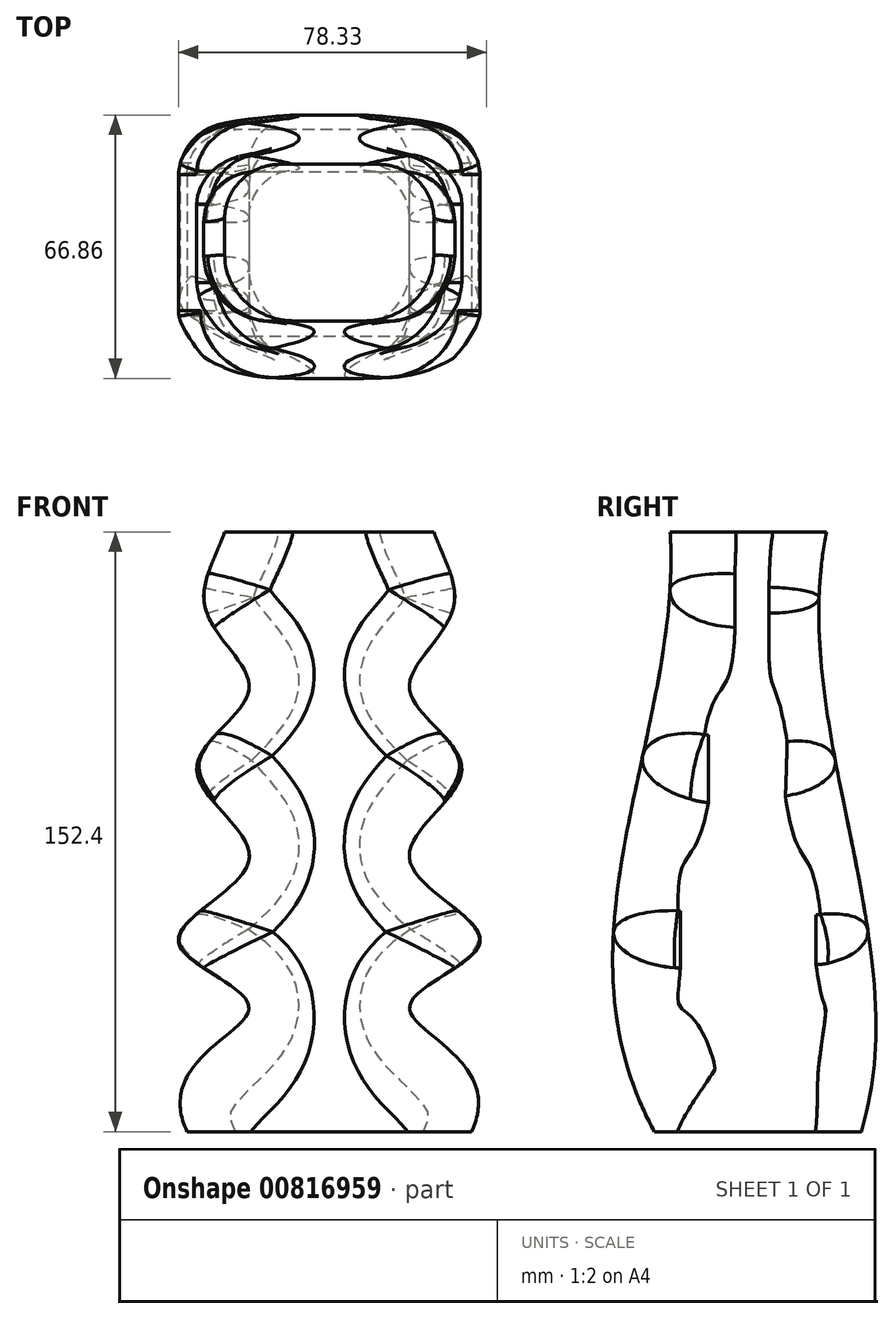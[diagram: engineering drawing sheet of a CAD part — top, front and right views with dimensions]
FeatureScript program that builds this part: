
annotation { "Feature Type Name" : "Feature", "Feature Type Description" : "" }
export const myFeature = defineFeature(function(context is Context, id is Id, definition is map)
    precondition{}
    {
        {
            var Q0;
            Q0=qCreatedBy(makeId("Top.planeOp"),FACE);
            var sketch = newSketch(context, id + "F0", { "sketchPlane" : qUnion([Q0])});
            skLineSegment(sketch, "E0.bottom", {"start": v(20.4, 44.64) * mm, "end": v(-20.4, 44.64) * mm});
            skLineSegment(sketch, "E0.top", {"start": v(20.4, -44.64) * mm, "end": v(-20.4, -44.64) * mm});
            skLineSegment(sketch, "E0.left", {"start": v(20.4, 44.64) * mm, "end": v(20.4, -44.64) * mm});
            skLineSegment(sketch, "E0.right", {"start": v(-20.4, 44.64) * mm, "end": v(-20.4, -44.64) * mm});
            skPoint(sketch, "E0.middle", {"position": v(0, 0) * mm});
            skSolve(sketch);
        }
        {
            var Q0;
            Q0=makeQuery(id+"F0.imprint","IMPRINT",FACE,{"disambiguationData":[TD([[makeQuery(id+"F0.imprint","IMPRINT",EDGE,{"derivedFrom":sQuery(id+"F0.wireOp",EDGE,"E0.bottom")}),1.0]])]});
            extrude(context, id + "F1", {"entities" : qUnion([Q0]), "depth" : 152.4 * mm, "offsetDistance" : 25.4 * mm});
        }
        {
            var Q0;
            Q0=makeQuery(id+"F1.opExtrude","SWEPT_FACE",FACE,{"disambiguationData":[OSD([sQuery(id+"F0.wireOp",EDGE,"E0.top")])]});
            var sketch = newSketch(context, id + "F2", { "sketchPlane" : qUnion([Q0])});
            skLineSegment(sketch, "E1.bottom", {"start": v(-29.62, 0) * mm, "end": v(31.26, 0) * mm});
            skLineSegment(sketch, "E1.top", {"start": v(-29.62, 170.24) * mm, "end": v(31.26, 170.24) * mm});
            skLineSegment(sketch, "E1.left", {"start": v(-29.62, 0) * mm, "end": v(-29.62, 170.24) * mm});
            skLineSegment(sketch, "E1.right", {"start": v(31.26, 0) * mm, "end": v(31.26, 170.24) * mm});
            skFitSpline(sketch, "E2", {"points": [v(10.39, 170.24) * mm, v(11.47, 135.65) * mm, v(0, 112.5) * mm, v(13.26, 91.93) * mm, v(0, 69.08) * mm, v(17.9, 48.24) * mm, v(0, 31.56) * mm, v(15.72, 0) * mm], "startDerivative": vector(-259.28, -196.56) * mm, "endDerivative": vector(-158.86, -332.78) * mm});
            skSolve(sketch);
        }
        {
            var Q0;
            {var subQ1=sQuery(id+"F0.wireOp",EDGE,"E0.top");var subQ2=makeQuery(id+"F1.opExtrude","SWEPT_EDGE",EDGE,{"disambiguationData":[OSD([subQ1,sQuery(id+"F0.wireOp",EDGE,"E0.left")])]});Q0=makeQuery(id+"F2.imprint","IMPRINT",FACE,{"disambiguationData":[TD([[makeQuery(id+"F2.imprint","IMPRINT",EDGE,{"derivedFrom":subQ2}),-1.0]])]});}
            extrude(context, id + "F3", {"entities" : qUnion([Q0]), "operationType" : NewBodyOperationType.REMOVE, "oppositeDirection" : true, "depth" : 336.04 * mm, "offsetDistance" : 25.4 * mm});
        }
        {
            var Q0;
            Q0=makeQuery(id+"F1.opExtrude","SWEPT_FACE",FACE,{"disambiguationData":[OSD([sQuery(id+"F0.wireOp",EDGE,"E0.right")])]});
            var sketch = newSketch(context, id + "F4", { "sketchPlane" : qUnion([Q0])});
            skFitSpline(sketch, "E3", {"points": [v(-24.75, 169.95) * mm, v(-27.8, 0) * mm], "startDerivative": vector(74.26, -161.1) * mm, "endDerivative": vector(48.86, -159.12) * mm});
            skFitSpline(sketch, "E4", {"points": [v(23.23, 169.19) * mm, v(24.75, 0) * mm], "startDerivative": vector(-41.48, -170.64) * mm, "endDerivative": vector(-90.8, -166.56) * mm});
            skSolve(sketch);
        }
        {
            var Q0;
            {var subQ1=sQuery(id+"F0.wireOp",EDGE,"E0.right");var subQ6=makeQuery(id+"F1.opExtrude","SWEPT_EDGE",EDGE,{"disambiguationData":[OSD([sQuery(id+"F0.wireOp",EDGE,"E0.top"),subQ1])]});Q0=makeQuery(id+"F4.imprint","IMPRINT",FACE,{"disambiguationData":[TD([[makeQuery(id+"F4.imprint","IMPRINT",EDGE,{"derivedFrom":subQ6}),-1.0]])]});}
            var Q1;
            {var subQ1=sQuery(id+"F0.wireOp",EDGE,"E0.right");var subQ6=makeQuery(id+"F1.opExtrude","SWEPT_EDGE",EDGE,{"disambiguationData":[OSD([sQuery(id+"F0.wireOp",EDGE,"E0.bottom"),subQ1])]});Q1=makeQuery(id+"F4.imprint","IMPRINT",FACE,{"disambiguationData":[TD([[makeQuery(id+"F4.imprint","IMPRINT",EDGE,{"derivedFrom":subQ6}),1.0]])]});}
            extrude(context, id + "F5", {"entities" : qUnion([Q0, Q1]), "operationType" : NewBodyOperationType.REMOVE, "oppositeDirection" : true, "depth" : 107.44 * mm, "offsetDistance" : 25.4 * mm});
        }
        {
            var Q0;
            Q0=makeQuery(id+"F1.opExtrude","SWEPT_BODY",BODY,{"disambiguationData":[OSD([sQuery(id+"F0.wireOp",EDGE,"E0.bottom"),sQuery(id+"F0.wireOp",EDGE,"E0.top"),sQuery(id+"F0.wireOp",EDGE,"E0.left"),sQuery(id+"F0.wireOp",EDGE,"E0.right")])]});
            var Q1;
            {var subQ0=sQuery(id+"F4.wireOp",EDGE,"E3");var subQ1=sQuery(id+"F0.wireOp",EDGE,"E0.right");var subQ2=makeQuery(id+"F1.opExtrude","CAP_EDGE",EDGE,{"disambiguationData":[OSD([subQ1])],"isStart":true});var subQ3=makeQuery(id+"F4.imprint","INTERSECT",VERTEX,{"derivedFrom":[subQ2,subQ0]});Q1=makeQuery(id+"F4.imprint","IMPRINT",FACE,{"disambiguationData":[TD([[makeQuery(id+"F4.imprint","IMPRINT",EDGE,{"disambiguationData":[TD([[subQ3,1.0]])],"derivedFrom":subQ0}),1.0]])]});}
            mirror(context, id + "F6", {"operationType" : NewBodyOperationType.ADD, "entities" : qUnion([Q0]), "mirrorPlane" : qUnion([Q1])});
        }
        {
            var Q0;
            Q0=makeQuery(id+"F6.opPattern","COPY",EDGE,{"derivedFrom":makeQuery(id+"F5.boolean.opBoolean","INTERSECT",EDGE,{"derivedFrom":[makeQuery(id+"F3.boolean.opBoolean","COPY",FACE,{"derivedFrom":makeQuery(id+"F3.opExtrude","SWEPT_FACE",FACE,{"disambiguationData":[OSD([sQuery(id+"F2.wireOp",EDGE,"E2")])]})}),makeQuery(id+"F5.opExtrude","SWEPT_FACE",FACE,{"disambiguationData":[OSD([sQuery(id+"F4.wireOp",EDGE,"E4")])]})]}),"instanceName":"1"});
            var Q1;
            Q1=makeQuery(id+"F5.boolean.opBoolean","INTERSECT",EDGE,{"derivedFrom":[makeQuery(id+"F3.boolean.opBoolean","COPY",FACE,{"derivedFrom":makeQuery(id+"F3.opExtrude","SWEPT_FACE",FACE,{"disambiguationData":[OSD([sQuery(id+"F2.wireOp",EDGE,"E2")])]})}),makeQuery(id+"F5.opExtrude","SWEPT_FACE",FACE,{"disambiguationData":[OSD([sQuery(id+"F4.wireOp",EDGE,"E4")])]})]});
            fillet(context, id + "F7", {"entities" : qUnion([Q0, Q1]), "radius" : 16.55 * mm, "tangentPropagation" : true, "allowEdgeOverflow" : false});
        }
        {
            var Q0;
            Q0=makeQuery(id+"F6.opPattern","COPY",EDGE,{"derivedFrom":makeQuery(id+"F5.boolean.opBoolean","INTERSECT",EDGE,{"derivedFrom":[makeQuery(id+"F3.boolean.opBoolean","COPY",FACE,{"derivedFrom":makeQuery(id+"F3.opExtrude","SWEPT_FACE",FACE,{"disambiguationData":[OSD([sQuery(id+"F2.wireOp",EDGE,"E2")])]})}),makeQuery(id+"F5.opExtrude","SWEPT_FACE",FACE,{"disambiguationData":[OSD([sQuery(id+"F4.wireOp",EDGE,"E3")])]})]}),"instanceName":"1"});
            var Q1;
            Q1=makeQuery(id+"F5.boolean.opBoolean","INTERSECT",EDGE,{"derivedFrom":[makeQuery(id+"F3.boolean.opBoolean","COPY",FACE,{"derivedFrom":makeQuery(id+"F3.opExtrude","SWEPT_FACE",FACE,{"disambiguationData":[OSD([sQuery(id+"F2.wireOp",EDGE,"E2")])]})}),makeQuery(id+"F5.opExtrude","SWEPT_FACE",FACE,{"disambiguationData":[OSD([sQuery(id+"F4.wireOp",EDGE,"E3")])]})]});
            fillet(context, id + "F8", {"entities" : qUnion([Q0, Q1]), "radius" : 12.7 * mm, "tangentPropagation" : true, "allowEdgeOverflow" : false});
        }
    });
